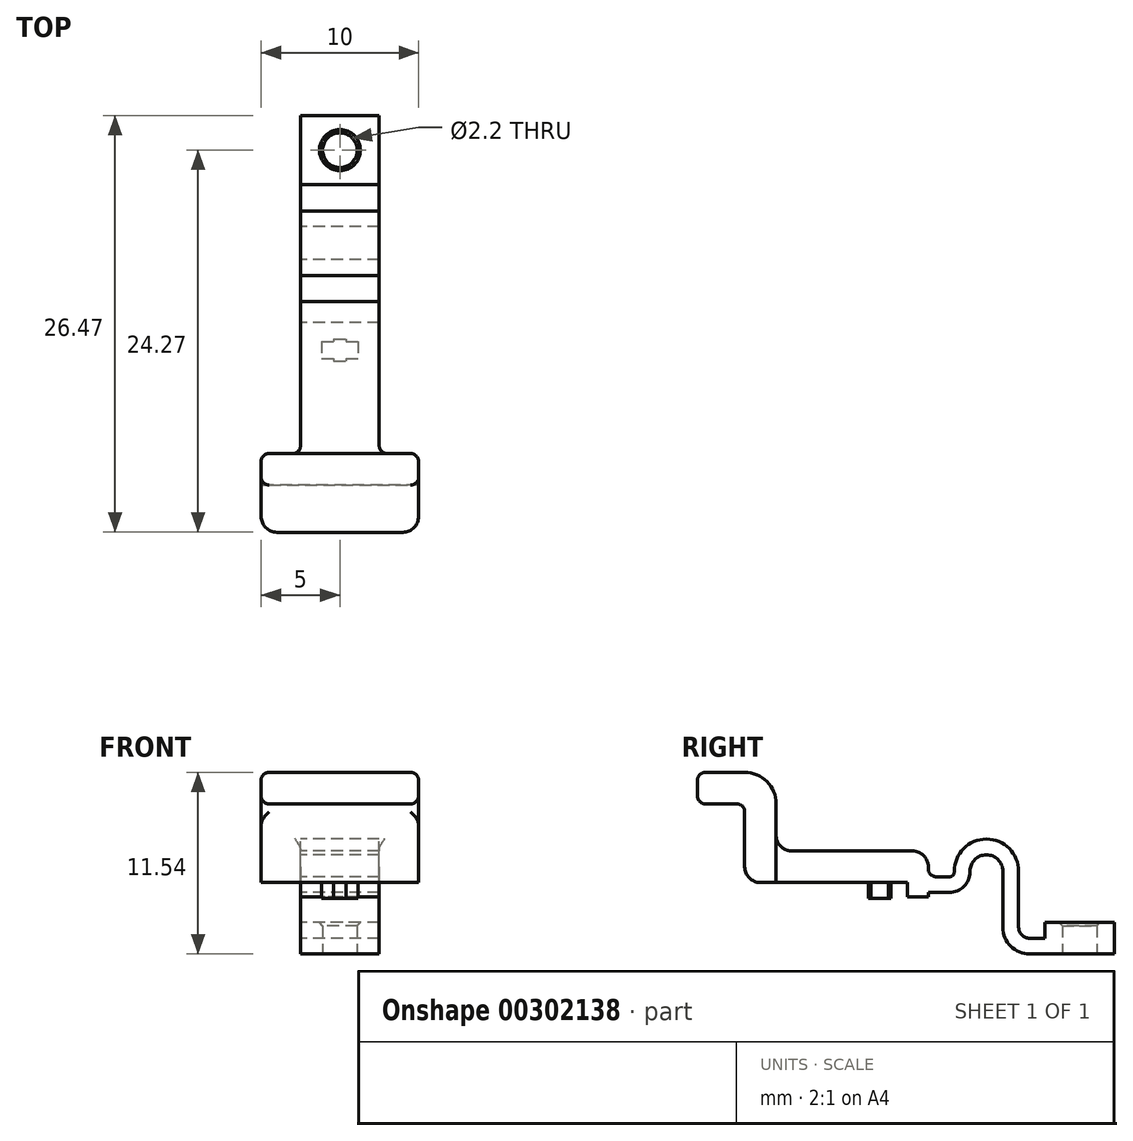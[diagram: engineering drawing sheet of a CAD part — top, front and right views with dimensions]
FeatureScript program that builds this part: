
annotation { "Feature Type Name" : "Feature", "Feature Type Description" : "" }
export const myFeature = defineFeature(function(context is Context, id is Id, definition is map)
    precondition{}
    {
        {
            var Q0;
            Q0=qCreatedBy(makeId("Top.planeOp"),FACE);
            var sketch = newSketch(context, id + "F0", { "sketchPlane" : qUnion([Q0])});
            skCircle(sketch, "E0", {"center": v(0, -0.86) * mm, "radius": 0.55 * mm});
            skCircle(sketch, "E1", {"center": v(0, 3.14) * mm, "radius": 0.55 * mm});
            skLineSegment(sketch, "E2.bottom", {"start": v(-2.4, 5.44) * mm, "end": v(2.4, 5.44) * mm});
            skLineSegment(sketch, "E2.top", {"start": v(-2.4, -3.16) * mm, "end": v(2.4, -3.16) * mm});
            skLineSegment(sketch, "E2.left", {"start": v(-2.4, 5.44) * mm, "end": v(-2.4, -3.16) * mm});
            skLineSegment(sketch, "E2.right", {"start": v(2.4, 5.44) * mm, "end": v(2.4, -3.16) * mm});
            skLineSegment(sketch, "E3.bottom", {"start": v(1.35, 0.5) * mm, "end": v(-1.35, 0.5) * mm});
            skLineSegment(sketch, "E3.top", {"start": v(1.35, -0.5) * mm, "end": v(-1.35, -0.5) * mm});
            skLineSegment(sketch, "E3.left", {"start": v(1.35, 0.5) * mm, "end": v(1.35, -0.5) * mm});
            skLineSegment(sketch, "E3.right", {"start": v(-1.35, 0.5) * mm, "end": v(-1.35, -0.5) * mm});
            skPoint(sketch, "E3.middle", {"position": v(0, 0) * mm});
            skPoint(sketch, "E4", {"position": v(2.4, 1.14) * mm});
            skLineSegment(sketch, "E5", {"start": v(0, 3.14) * mm, "end": v(0, -0.86) * mm, "construction": true});
            skPoint(sketch, "E6", {"position": v(0, 1.14) * mm});
            skLineSegment(sketch, "E7", {"start": v(2.4, 1.14) * mm, "end": v(0.81, 1.14) * mm, "construction": true});
            skPoint(sketch, "E8", {"position": v(0, 5.44) * mm});
            skSolve(sketch);
        }
        {
            var Q0;
            Q0=qCreatedBy(makeId("Top.planeOp"),FACE);
            var sketch = newSketch(context, id + "F1", { "sketchPlane" : qUnion([Q0])});
            skCircle(sketch, "E9", {"center": v(0, 12.7) * mm, "radius": 1.1 * mm});
            skCircle(sketch, "E10", {"center": v(0, 12.7) * mm, "radius": 1.75 * mm, "construction": true});
            skSolve(sketch);
        }
        {
            var Q0;
            Q0=qCreatedBy(makeId("Right.planeOp"),FACE);
            var sketch = newSketch(context, id + "F2", { "sketchPlane" : qUnion([Q0])});
            skLineSegment(sketch, "E11.bottom", {"start": v(-8.57, 6.54) * mm, "end": v(3.1, 6.54) * mm});
            skLineSegment(sketch, "E11.top", {"start": v(-8.57, 4.54) * mm, "end": v(1.76, 4.54) * mm});
            skLineSegment(sketch, "E11.left", {"start": v(-8.57, 6.54) * mm, "end": v(-8.57, 4.54) * mm});
            skLineSegment(sketch, "E11.right", {"start": v(3.1, 6.54) * mm, "end": v(3.1, 4.54) * mm});
            skLineSegment(sketch, "E12.bottom", {"start": v(10.5, 2) * mm, "end": v(14.9, 2) * mm});
            skLineSegment(sketch, "E12.top", {"start": v(10.5, 0) * mm, "end": v(14.9, 0) * mm});
            skLineSegment(sketch, "E12.left", {"start": v(10.5, 2) * mm, "end": v(10.5, 0) * mm});
            skLineSegment(sketch, "E12.right", {"start": v(14.9, 2) * mm, "end": v(14.9, 0) * mm});
            skLineSegment(sketch, "E13", {"start": v(-6.3, 2.66) * mm, "end": v(-6.3, 0.53) * mm, "construction": true});
            skPoint(sketch, "E14", {"position": v(0, 4.54) * mm});
            skLineSegment(sketch, "E15", {"start": v(3.1, 4.4) * mm, "end": v(4.44, 4.4) * mm});
            skLineSegment(sketch, "E16", {"start": v(5.24, 5.2) * mm, "end": v(5.24, 5.25) * mm});
            skLineSegment(sketch, "E17", {"start": v(8.33, 5.25) * mm, "end": v(8.33, 1.7) * mm});
            skLineSegment(sketch, "E18", {"start": v(9.53, 0.5) * mm, "end": v(10.5, 0.5) * mm});
            skPoint(sketch, "E19.visualSharp", {"position": v(5.24, 4.4) * mm});
            skArc(sketch, "E19.filletArc", {"start": v(4.44, 4.4) * mm, "mid": v(5, 4.64) * mm, "end": v(5.24, 5.2) * mm});
            skArc(sketch, "E20.filletArc", {"start": v(8.33, 5.25) * mm, "mid": v(6.79, 6.8) * mm, "end": v(5.24, 5.25) * mm});
            skPoint(sketch, "E21.visualSharp", {"position": v(8.33, 0.5) * mm});
            skArc(sketch, "E21.filletArc", {"start": v(8.33, 1.7) * mm, "mid": v(8.68, 0.85) * mm, "end": v(9.53, 0.5) * mm});
            skLineSegment(sketch, "E22", {"start": v(6.79, 5.25) * mm, "end": v(7.52, 5.25) * mm, "construction": true});
            skPoint(sketch, "E23", {"position": v(6.79, 6.8) * mm});
            skLineSegment(sketch, "E24", {"start": v(3.1, 4.54) * mm, "end": v(3.1, 3.62) * mm});
            skLineSegment(sketch, "E25", {"start": v(3.1, 3.62) * mm, "end": v(1.76, 3.62) * mm});
            skLineSegment(sketch, "E26", {"start": v(1.76, 3.62) * mm, "end": v(1.76, 4.54) * mm});
            skSolve(sketch);
        }
        {
            var Q0;
            Q0=qSketchRegion(id+"F2",true);
            extrude(context, id + "F3", {"entities" : qUnion([Q0]), "endBound" : BoundingType.SYMMETRIC, "depth" : 5 * mm});
        }
        {
            var Q0;
            Q0=sQuery(id+"F2.wireOp",VERTEX,"E15.start");
            var Q1;
            Q1=sQuery(id+"F2.wireOp",EDGE,"E15");
            cPlane(context, id + "F4", {"entities" : qUnion([Q0, Q1]), "cplaneType" : CPlaneType.CURVE_POINT, "offset" : 25 * mm, "width" : 150 * mm, "height" : 150 * mm});
        }
        {
            var Q0;
            Q0=qCreatedBy(id+"F4.planeOp",FACE);
            var sketch = newSketch(context, id + "F5", { "sketchPlane" : qUnion([Q0])});
            skLineSegment(sketch, "E27.bottom", {"start": v(-2.5, 4.9) * mm, "end": v(2.5, 4.9) * mm});
            skLineSegment(sketch, "E27.top", {"start": v(-2.5, 3.9) * mm, "end": v(2.5, 3.9) * mm});
            skLineSegment(sketch, "E27.left", {"start": v(-2.5, 4.9) * mm, "end": v(-2.5, 3.9) * mm});
            skLineSegment(sketch, "E27.right", {"start": v(2.5, 4.9) * mm, "end": v(2.5, 3.9) * mm});
            skPoint(sketch, "E27.middle", {"position": v(0, 4.4) * mm});
            skSolve(sketch);
        }
        {
            var Q0;
            Q0=qSketchRegion(id+"F5",true);
            var Q1;
            Q1=sQuery(id+"F2.wireOp",EDGE,"E15");
            var Q2;
            Q2=sQuery(id+"F2.wireOp",EDGE,"E19.filletArc");
            var Q3;
            Q3=sQuery(id+"F2.wireOp",EDGE,"E16");
            var Q4;
            Q4=sQuery(id+"F2.wireOp",EDGE,"E20.filletArc");
            var Q5;
            Q5=sQuery(id+"F2.wireOp",EDGE,"3BrdmAZu-ONtJ-KdVl-KuM2-4Njug2Lyjafy");
            var Q6;
            Q6=sQuery(id+"F2.wireOp",EDGE,"c1a8fe4b-899e-4b09-802d-e28b608389ea.filletArc");
            var Q7;
            Q7=sQuery(id+"F2.wireOp",EDGE,"E17");
            var Q8;
            Q8=sQuery(id+"F2.wireOp",EDGE,"E21.filletArc");
            var Q9;
            Q9=sQuery(id+"F2.wireOp",EDGE,"E18");
            sweep(context, id + "F6", {"operationType" : NewBodyOperationType.ADD, "profiles" : qUnion([Q0]), "path" : qUnion([Q1, Q2, Q3, Q4, Q5, Q6, Q7, Q8, Q9])});
        }
        {
            var Q0;
            Q0=qSketchRegion(id+"F1",true);
            extrude(context, id + "F7", {"entities" : qUnion([Q0]), "operationType" : NewBodyOperationType.REMOVE, "depth" : 25 * mm});
        }
        {
            var Q0;
            Q0=makeQuery(id+"F3.opExtrude","SWEPT_FACE",FACE,{"disambiguationData":[OSD([sQuery(id+"F2.wireOp",EDGE,"E11.top")])]});
            var sketch = newSketch(context, id + "F8", { "sketchPlane" : qUnion([Q0])});
            skLineSegment(sketch, "E28.bottom", {"start": v(-0.4, -0.7) * mm, "end": v(0.4, -0.7) * mm});
            skLineSegment(sketch, "E28.top", {"start": v(-0.4, 0.7) * mm, "end": v(0.4, 0.7) * mm});
            skLineSegment(sketch, "E28.left", {"start": v(-0.4, -0.7) * mm, "end": v(-0.4, 0.7) * mm});
            skLineSegment(sketch, "E28.right", {"start": v(0.4, -0.7) * mm, "end": v(0.4, 0.7) * mm});
            skPoint(sketch, "E28.middle", {"position": v(0, 0) * mm});
            skLineSegment(sketch, "E29.bottom", {"start": v(-1.15, -0.55) * mm, "end": v(1.15, -0.55) * mm});
            skLineSegment(sketch, "E29.top", {"start": v(-1.15, 0.55) * mm, "end": v(1.15, 0.55) * mm});
            skLineSegment(sketch, "E29.left", {"start": v(-1.15, -0.55) * mm, "end": v(-1.15, 0.55) * mm});
            skLineSegment(sketch, "E29.right", {"start": v(1.15, -0.55) * mm, "end": v(1.15, 0.55) * mm});
            skSolve(sketch);
        }
        {
            var Q0;
            Q0=qSketchRegion(id+"F8",true);
            extrude(context, id + "F9", {"entities" : qUnion([Q0]), "operationType" : NewBodyOperationType.ADD, "depth" : 1 * mm});
        }
        {
            var Q0;
            Q0=makeQuery(id+"F6.opSweep","CAP_EDGE",EDGE,{"disambiguationData":[OSD([sQuery(id+"F2.wireOp",VERTEX,"E18.end"),sQuery(id+"F5.wireOp",EDGE,"E27.bottom")])],"isStart":false});
            var Q1;
            Q1=makeQuery(id+"F6.opSweep","CAP_EDGE",EDGE,{"disambiguationData":[OSD([sQuery(id+"F2.wireOp",VERTEX,"E18.end"),sQuery(id+"F5.wireOp",EDGE,"E27.top")])],"isStart":false});
            var Q2;
            Q2=makeQuery(id+"F6.opSweep","CAP_EDGE",EDGE,{"disambiguationData":[OSD([sQuery(id+"F2.wireOp",VERTEX,"E15.start"),sQuery(id+"F5.wireOp",EDGE,"E27.bottom")])],"isStart":true});
            var Q3;
            Q3=makeQuery(id+"F6.opSweep","CAP_EDGE",EDGE,{"disambiguationData":[OSD([sQuery(id+"F2.wireOp",VERTEX,"E15.start"),sQuery(id+"F5.wireOp",EDGE,"E27.top")])],"isStart":true});
            fillet(context, id + "F10", {"entities" : qUnion([Q0, Q1, Q2, Q3]), "radius" : 0.5 * mm, "tangentPropagation" : true, "allowEdgeOverflow" : false});
        }
        {
            var Q0;
            Q0=makeQuery(id+"F7.boolean.opBoolean","INTERSECT",EDGE,{"derivedFrom":[makeQuery(id+"F3.opExtrude","SWEPT_FACE",FACE,{"disambiguationData":[OSD([sQuery(id+"F2.wireOp",EDGE,"E12.bottom")])]}),makeQuery(id+"F7.opExtrude","SWEPT_FACE",FACE,{"disambiguationData":[OSD([sQuery(id+"F1.wireOp",EDGE,"E9")])]})]});
            var Q1;
            Q1=makeQuery(id+"F7.boolean.opBoolean","COPY",EDGE,{"derivedFrom":makeQuery(id+"F7.opExtrude","CAP_EDGE",EDGE,{"disambiguationData":[OSD([sQuery(id+"F1.wireOp",EDGE,"E9")])],"isStart":true})});
            chamfer(context, id + "F11", {"entities" : qUnion([Q0, Q1]), "width" : 0.2 * mm, "tangentPropagation" : true});
        }
        {
            var Q0;
            Q0=makeQuery(id+"F3.opExtrude","SWEPT_FACE",FACE,{"disambiguationData":[OSD([sQuery(id+"F2.wireOp",EDGE,"E11.bottom")])]});
            var sketch = newSketch(context, id + "F12", { "sketchPlane" : qUnion([Q0])});
            skLineSegment(sketch, "E30.bottom", {"start": v(5, -6.57) * mm, "end": v(-5, -6.57) * mm});
            skLineSegment(sketch, "E30.top", {"start": v(5, -8.57) * mm, "end": v(-5, -8.57) * mm});
            skLineSegment(sketch, "E30.left", {"start": v(5, -6.57) * mm, "end": v(5, -8.57) * mm});
            skLineSegment(sketch, "E30.right", {"start": v(-5, -6.57) * mm, "end": v(-5, -8.57) * mm});
            skPoint(sketch, "E30.middle", {"position": v(0, -7.57) * mm});
            skSolve(sketch);
        }
        {
            var Q0;
            Q0=qSketchRegion(id+"F12",true);
            var Q1;
            Q1=makeQuery(id+"F3.opExtrude","SWEPT_FACE",FACE,{"disambiguationData":[OSD([sQuery(id+"F2.wireOp",EDGE,"E11.top")])]});
            extrude(context, id + "F13", {"entities" : qUnion([Q0]), "operationType" : NewBodyOperationType.ADD, "endBound" : BoundingType.UP_TO_SURFACE, "oppositeDirection" : true, "endBoundEntityFace" : qUnion([Q1]), "depth" : 25 * mm, "hasSecondDirection" : true, "secondDirectionOppositeDirection" : false, "secondDirectionDepth" : 5 * mm});
        }
        {
            var Q0;
            Q0=makeQuery(id+"F13.boolean.opBoolean","MERGE",FACE,{"derivedFrom":[makeQuery(id+"F3.opExtrude","SWEPT_FACE",FACE,{"disambiguationData":[OSD([sQuery(id+"F2.wireOp",EDGE,"E11.left")])]}),makeQuery(id+"F13.opExtrude","SWEPT_FACE",FACE,{"disambiguationData":[OSD([sQuery(id+"F12.wireOp",EDGE,"E30.top")])]})]});
            var sketch = newSketch(context, id + "F14", { "sketchPlane" : qUnion([Q0])});
            skLineSegment(sketch, "E31.bottom", {"start": v(-5, 11.54) * mm, "end": v(5, 11.54) * mm});
            skLineSegment(sketch, "E31.top", {"start": v(-5, 9.54) * mm, "end": v(5, 9.54) * mm});
            skLineSegment(sketch, "E31.left", {"start": v(-5, 11.54) * mm, "end": v(-5, 9.54) * mm});
            skLineSegment(sketch, "E31.right", {"start": v(5, 11.54) * mm, "end": v(5, 9.54) * mm});
            skSolve(sketch);
        }
        {
            var Q0;
            Q0=qSketchRegion(id+"F14",true);
            extrude(context, id + "F15", {"entities" : qUnion([Q0]), "operationType" : NewBodyOperationType.ADD, "depth" : 3 * mm});
        }
        {
            var Q0;
            Q0=makeQuery(id+"F13.opExtrude","CAP_EDGE",EDGE,{"disambiguationData":[OSD([sQuery(id+"F12.wireOp",EDGE,"E30.bottom")])],"isStart":true});
            fillet(context, id + "F16", {"entities" : qUnion([Q0]), "radius" : 2 * mm, "tangentPropagation" : true, "allowEdgeOverflow" : false});
        }
        {
            var Q0;
            Q0=makeQuery(id+"F15.opExtrude","CAP_EDGE",EDGE,{"disambiguationData":[OSD([sQuery(id+"F14.wireOp",EDGE,"E31.right")])],"isStart":false});
            var Q1;
            Q1=makeQuery(id+"F15.opExtrude","CAP_EDGE",EDGE,{"disambiguationData":[OSD([sQuery(id+"F14.wireOp",EDGE,"E31.left")])],"isStart":false});
            fillet(context, id + "F17", {"entities" : qUnion([Q0, Q1]), "radius" : 1 * mm, "tangentPropagation" : true, "allowEdgeOverflow" : false});
        }
        {
            var Q0;
            Q0=makeQuery(id+"F15.boolean.opBoolean","MERGE",FACE,{"derivedFrom":[makeQuery(id+"F13.opExtrude","CAP_FACE",FACE,{"disambiguationData":[OSD([sQuery(id+"F12.wireOp",EDGE,"E30.bottom"),sQuery(id+"F12.wireOp",EDGE,"E30.top"),sQuery(id+"F12.wireOp",EDGE,"E30.left"),sQuery(id+"F12.wireOp",EDGE,"E30.right")])],"isStart":true}),makeQuery(id+"F15.opExtrude","SWEPT_FACE",FACE,{"disambiguationData":[OSD([sQuery(id+"F14.wireOp",EDGE,"E31.bottom")])]})]});
            fillet(context, id + "F18", {"entities" : qUnion([Q0]), "radius" : 0.5 * mm, "tangentPropagation" : true, "allowEdgeOverflow" : false});
        }
        {
            var Q0;
            Q0=makeQuery(id+"F13.boolean.opBoolean","INTERSECT",EDGE,{"derivedFrom":[makeQuery(id+"F3.opExtrude","SWEPT_FACE",FACE,{"disambiguationData":[OSD([sQuery(id+"F2.wireOp",EDGE,"E11.bottom")])]}),makeQuery(id+"F13.opExtrude","SWEPT_FACE",FACE,{"disambiguationData":[OSD([sQuery(id+"F12.wireOp",EDGE,"E30.bottom")])]})]});
            var Q1;
            {var subQ0=sQuery(id+"F12.wireOp",EDGE,"E30.top");var subQ1=sQuery(id+"F2.wireOp",EDGE,"E11.bottom");var subQ2=makeQuery(id+"F12.imprint","INTERSECT",VERTEX,{"derivedFrom":[makeQuery(id+"F3.opExtrude","CAP_EDGE",EDGE,{"disambiguationData":[OSD([subQ1])],"isStart":true}),subQ0]});var subQ3=makeQuery(id+"F12.imprint","INTERSECT",VERTEX,{"derivedFrom":[makeQuery(id+"F3.opExtrude","CAP_EDGE",EDGE,{"disambiguationData":[OSD([subQ1])],"isStart":false}),subQ0]});var subQ4=sQuery(id+"F2.wireOp",EDGE,"E11.top");Q1=makeQuery(id+"F13.boolean.opBoolean","MERGE",EDGE,{"derivedFrom":[makeQuery(id+"F3.opExtrude","SWEPT_EDGE",EDGE,{"disambiguationData":[OSD([subQ4,sQuery(id+"F2.wireOp",EDGE,"E11.left")])]}),makeQuery(id+"F13.opExtrude","TWEAK_EDGE",EDGE,{"derivedFrom":[makeQuery(id+"F3.opExtrude","SWEPT_FACE",FACE,{"disambiguationData":[OSD([subQ4])]}),makeQuery(id+"F12.imprint","IMPRINT",EDGE,{"disambiguationData":[TD([[subQ3,1.0]])],"derivedFrom":subQ0}),makeQuery(id+"F12.imprint","IMPRINT",EDGE,{"disambiguationData":[TD([[subQ2,1.0]])],"derivedFrom":subQ0}),makeQuery(id+"F12.imprint","IMPRINT",EDGE,{"disambiguationData":[TD([[subQ2,-1.0]])],"derivedFrom":subQ0})]})]});}
            fillet(context, id + "F19", {"entities" : qUnion([Q0, Q1]), "radius" : 1 * mm, "tangentPropagation" : true, "allowEdgeOverflow" : false});
        }
        {
            var Q0;
            Q0=makeQuery(id+"F13.boolean.opBoolean","INTERSECT",EDGE,{"derivedFrom":[makeQuery(id+"F6.boolean.opBoolean","MERGE",FACE,{"derivedFrom":[makeQuery(id+"F3.opExtrude","CAP_FACE",FACE,{"disambiguationData":[OSD([sQuery(id+"F2.wireOp",EDGE,"E11.bottom"),sQuery(id+"F2.wireOp",EDGE,"E11.top"),sQuery(id+"F2.wireOp",EDGE,"E11.left"),sQuery(id+"F2.wireOp",EDGE,"E11.right"),sQuery(id+"F2.wireOp",EDGE,"E24"),sQuery(id+"F2.wireOp",EDGE,"E25"),sQuery(id+"F2.wireOp",EDGE,"E26")])],"isStart":false}),makeQuery(id+"F3.opExtrude","CAP_FACE",FACE,{"disambiguationData":[OSD([sQuery(id+"F2.wireOp",EDGE,"E12.bottom"),sQuery(id+"F2.wireOp",EDGE,"E12.top"),sQuery(id+"F2.wireOp",EDGE,"E12.left"),sQuery(id+"F2.wireOp",EDGE,"E12.right")])],"isStart":false}),makeQuery(id+"F6.opSweep","SWEPT_FACE",FACE,{"disambiguationData":[OSD([sQuery(id+"F2.wireOp",EDGE,"E15"),sQuery(id+"F5.wireOp",EDGE,"E27.left")])]})]}),makeQuery(id+"F13.opExtrude","SWEPT_FACE",FACE,{"disambiguationData":[OSD([sQuery(id+"F12.wireOp",EDGE,"E30.bottom")])]})]});
            var Q1;
            Q1=makeQuery(id+"F13.boolean.opBoolean","INTERSECT",EDGE,{"derivedFrom":[makeQuery(id+"F6.boolean.opBoolean","MERGE",FACE,{"derivedFrom":[makeQuery(id+"F3.opExtrude","CAP_FACE",FACE,{"disambiguationData":[OSD([sQuery(id+"F2.wireOp",EDGE,"E11.bottom"),sQuery(id+"F2.wireOp",EDGE,"E11.top"),sQuery(id+"F2.wireOp",EDGE,"E11.left"),sQuery(id+"F2.wireOp",EDGE,"E11.right"),sQuery(id+"F2.wireOp",EDGE,"E24"),sQuery(id+"F2.wireOp",EDGE,"E25"),sQuery(id+"F2.wireOp",EDGE,"E26")])],"isStart":true}),makeQuery(id+"F3.opExtrude","CAP_FACE",FACE,{"disambiguationData":[OSD([sQuery(id+"F2.wireOp",EDGE,"E12.bottom"),sQuery(id+"F2.wireOp",EDGE,"E12.top"),sQuery(id+"F2.wireOp",EDGE,"E12.left"),sQuery(id+"F2.wireOp",EDGE,"E12.right")])],"isStart":true}),makeQuery(id+"F6.opSweep","SWEPT_FACE",FACE,{"disambiguationData":[OSD([sQuery(id+"F2.wireOp",EDGE,"E15"),sQuery(id+"F5.wireOp",EDGE,"E27.right")])]})]}),makeQuery(id+"F13.opExtrude","SWEPT_FACE",FACE,{"disambiguationData":[OSD([sQuery(id+"F12.wireOp",EDGE,"E30.bottom")])]})]});
            var Q2;
            Q2=makeQuery(id+"F15.opExtrude","CAP_EDGE",EDGE,{"disambiguationData":[OSD([sQuery(id+"F14.wireOp",EDGE,"E31.top")])],"isStart":true});
            var Q3;
            Q3=makeQuery(id+"F15.opExtrude","SWEPT_FACE",FACE,{"disambiguationData":[OSD([sQuery(id+"F14.wireOp",EDGE,"E31.top")])]});
            fillet(context, id + "F20", {"entities" : qUnion([Q0, Q1, Q2, Q3]), "radius" : 0.5 * mm, "tangentPropagation" : true, "allowEdgeOverflow" : false});
        }
        {
            var Q0;
            Q0=makeQuery(id+"F3.opExtrude","SWEPT_EDGE",EDGE,{"disambiguationData":[OSD([sQuery(id+"F2.wireOp",EDGE,"E11.bottom"),sQuery(id+"F2.wireOp",EDGE,"E11.right")])]});
            fillet(context, id + "F21", {"entities" : qUnion([Q0]), "radius" : 1 * mm, "tangentPropagation" : true, "allowEdgeOverflow" : false});
        }
    });
